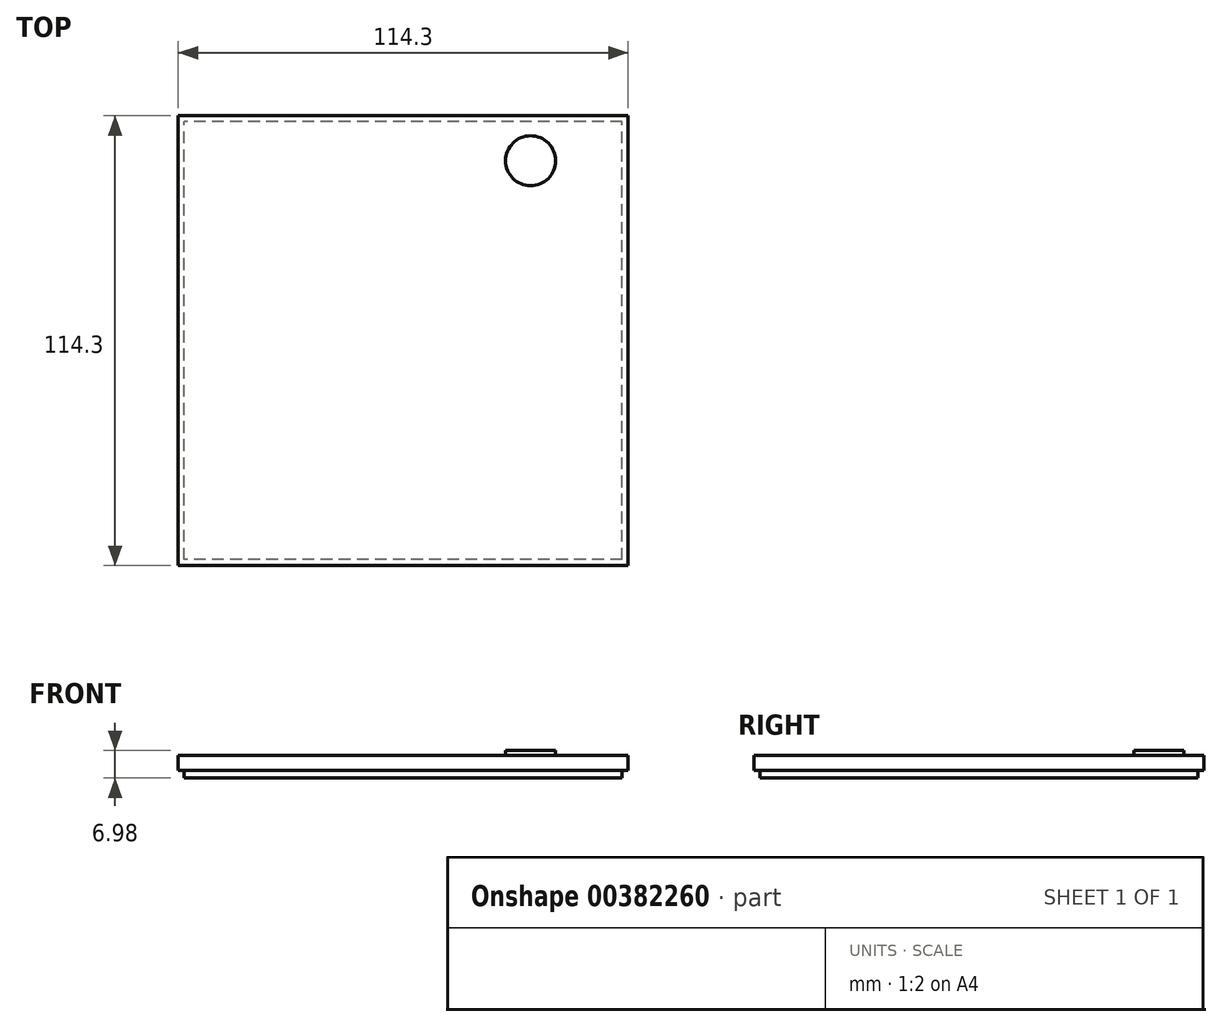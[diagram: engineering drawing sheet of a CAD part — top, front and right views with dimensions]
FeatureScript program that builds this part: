
annotation { "Feature Type Name" : "Feature", "Feature Type Description" : "" }
export const myFeature = defineFeature(function(context is Context, id is Id, definition is map)
    precondition{}
    {
        {
            var Q0;
            Q0=qCreatedBy(makeId("Top.planeOp"),FACE);
            var sketch = newSketch(context, id + "F0", { "sketchPlane" : qUnion([Q0])});
            skLineSegment(sketch, "E0.bottom", {"start": v(57.15, 57.15) * mm, "end": v(-57.15, 57.15) * mm});
            skLineSegment(sketch, "E0.top", {"start": v(57.15, -57.15) * mm, "end": v(-57.15, -57.15) * mm});
            skLineSegment(sketch, "E0.left", {"start": v(57.15, 57.15) * mm, "end": v(57.15, -57.15) * mm});
            skLineSegment(sketch, "E0.right", {"start": v(-57.15, 57.15) * mm, "end": v(-57.15, -57.15) * mm});
            skPoint(sketch, "E0.middle", {"position": v(0, 0) * mm});
            skSolve(sketch);
        }
        {
            var Q0;
            Q0=makeQuery(id+"F0.imprint","IMPRINT",FACE,{"disambiguationData":[TD([[makeQuery(id+"F0.imprint","IMPRINT",EDGE,{"derivedFrom":sQuery(id+"F0.wireOp",EDGE,"E0.bottom")}),1.0]])]});
            extrude(context, id + "F1", {"entities" : qUnion([Q0]), "depth" : 2.54 * mm});
        }
        {
            var Q0;
            Q0=makeQuery(id+"F1.opExtrude","SWEPT_FACE",FACE,{"disambiguationData":[OSD([sQuery(id+"F0.wireOp",EDGE,"E0.left")])]});
            var sketch = newSketch(context, id + "F2", { "sketchPlane" : qUnion([Q0])});
            skLineSegment(sketch, "E1.bottom", {"start": v(-57.15, 0) * mm, "end": v(57.15, 0) * mm});
            skLineSegment(sketch, "E2.top", {"start": v(-57.15, 27.94) * mm, "end": v(57.15, 27.94) * mm});
            skLineSegment(sketch, "E2.left", {"start": v(-57.15, 2.54) * mm, "end": v(-57.15, 27.94) * mm});
            skLineSegment(sketch, "E2.right", {"start": v(57.15, 2.54) * mm, "end": v(57.15, 27.94) * mm});
            skSolve(sketch);
        }
        {
            var Q0;
            Q0=makeQuery(id+"F2.imprint","IMPRINT",FACE,{"disambiguationData":[TD([[makeQuery(id+"F2.imprint","IMPRINT",EDGE,{"derivedFrom":sQuery(id+"F2.wireOp",EDGE,"E2.top")}),-1.0]])]});
            extrude(context, id + "F3", {"entities" : qUnion([Q0]), "oppositeDirection" : true, "depth" : 2.54 * mm});
        }
        {
            var Q0;
            Q0=makeQuery(id+"F3.opExtrude","SWEPT_BODY",BODY,{"disambiguationData":[OSD([sQuery(id+"F0.wireOp",EDGE,"E0.left"),sQuery(id+"F2.wireOp",EDGE,"E2.top"),sQuery(id+"F2.wireOp",EDGE,"E2.left"),sQuery(id+"F2.wireOp",EDGE,"E2.right")])]});
            var Q1;
            Q1=qCreatedBy(makeId("Right.planeOp"),FACE);
            mirror(context, id + "F4", {"operationType" : NewBodyOperationType.ADD, "entities" : qUnion([Q0]), "mirrorPlane" : qUnion([Q1])});
        }
        {
            var Q0;
            {var subQ0=makeQuery(id+"F3.opExtrude","SWEPT_FACE",FACE,{"disambiguationData":[OSD([sQuery(id+"F2.wireOp",EDGE,"E2.right")])]});Q0=makeQuery(id+"F4.boolean.opBoolean","MERGE",FACE,{"derivedFrom":[makeQuery(id+"F1.opExtrude","SWEPT_FACE",FACE,{"disambiguationData":[OSD([sQuery(id+"F0.wireOp",EDGE,"E0.bottom")])]}),subQ0,makeQuery(id+"F4.opPattern","COPY",FACE,{"derivedFrom":subQ0,"instanceName":"1"})]});}
            var sketch = newSketch(context, id + "F5", { "sketchPlane" : qUnion([Q0])});
            skLineSegment(sketch, "E3.bottom", {"start": v(-54.61, 2.54) * mm, "end": v(54.61, 2.54) * mm});
            skLineSegment(sketch, "E3.top", {"start": v(-54.61, 27.94) * mm, "end": v(54.61, 27.94) * mm});
            skLineSegment(sketch, "E3.left", {"start": v(-54.61, 2.54) * mm, "end": v(-54.61, 27.94) * mm});
            skLineSegment(sketch, "E3.right", {"start": v(54.61, 2.54) * mm, "end": v(54.61, 27.94) * mm});
            skSolve(sketch);
        }
        {
            var Q0;
            Q0=makeQuery(id+"F5.imprint","IMPRINT",FACE,{"disambiguationData":[TD([[makeQuery(id+"F5.imprint","IMPRINT",EDGE,{"derivedFrom":sQuery(id+"F5.wireOp",EDGE,"E3.bottom")}),1.0]])]});
            extrude(context, id + "F6", {"entities" : qUnion([Q0]), "oppositeDirection" : true, "depth" : 2.54 * mm});
        }
        {
            var Q0;
            Q0=makeQuery(id+"F6.opExtrude","SWEPT_BODY",BODY,{"disambiguationData":[OSD([sQuery(id+"F5.wireOp",EDGE,"E3.bottom"),sQuery(id+"F5.wireOp",EDGE,"E3.top"),sQuery(id+"F5.wireOp",EDGE,"E3.left"),sQuery(id+"F5.wireOp",EDGE,"E3.right")])]});
            var Q1;
            Q1=qCreatedBy(makeId("Front.planeOp"),FACE);
            mirror(context, id + "F7", {"operationType" : NewBodyOperationType.ADD, "entities" : qUnion([Q0]), "mirrorPlane" : qUnion([Q1])});
        }
        {
            var Q0;
            {var subQ0=makeQuery(id+"F6.opExtrude","SWEPT_FACE",FACE,{"disambiguationData":[OSD([sQuery(id+"F5.wireOp",EDGE,"E3.top")])]});var subQ1=makeQuery(id+"F3.opExtrude","SWEPT_FACE",FACE,{"disambiguationData":[OSD([sQuery(id+"F2.wireOp",EDGE,"E2.top")])]});Q0=makeQuery(id+"F7.boolean.opBoolean","MERGE",FACE,{"derivedFrom":[subQ1,makeQuery(id+"F4.opPattern","COPY",FACE,{"derivedFrom":subQ1,"instanceName":"1"}),subQ0,makeQuery(id+"F7.opPattern","COPY",FACE,{"derivedFrom":subQ0,"instanceName":"1"})]});}
            var sketch = newSketch(context, id + "F8", { "sketchPlane" : qUnion([Q0])});
            skLineSegment(sketch, "E4.bottom", {"start": v(57.15, 57.15) * mm, "end": v(-57.15, 57.15) * mm});
            skLineSegment(sketch, "E4.top", {"start": v(57.15, -57.15) * mm, "end": v(-57.15, -57.15) * mm});
            skLineSegment(sketch, "E4.left", {"start": v(57.15, 57.15) * mm, "end": v(57.15, -57.15) * mm});
            skLineSegment(sketch, "E4.right", {"start": v(-57.15, 57.15) * mm, "end": v(-57.15, -57.15) * mm});
            skSolve(sketch);
        }
        {
            var Q0;
            Q0=makeQuery(id+"F8.imprint","IMPRINT",FACE,{"disambiguationData":[TD([[makeQuery(id+"F8.imprint","IMPRINT",EDGE,{"derivedFrom":sQuery(id+"F8.wireOp",EDGE,"E4.bottom")}),-1.0]])]});
            var Q1;
            {var subQ0=makeQuery(id+"F6.opExtrude","CAP_EDGE",EDGE,{"disambiguationData":[OSD([sQuery(id+"F5.wireOp",EDGE,"E3.top")])],"isStart":false});Q1=makeQuery(id+"F8.imprint","IMPRINT",FACE,{"disambiguationData":[TD([[makeQuery(id+"F8.imprint","IMPRINT",EDGE,{"derivedFrom":subQ0}),1.0]])]});}
            extrude(context, id + "F9", {"entities" : qUnion([Q0, Q1]), "depth" : 2.54 * mm});
        }
        {
            var Q0;
            Q0=makeQuery(id+"F9.opExtrude","CAP_FACE",FACE,{"disambiguationData":[OSD([sQuery(id+"F8.wireOp",EDGE,"E4.bottom"),sQuery(id+"F8.wireOp",EDGE,"E4.top"),sQuery(id+"F8.wireOp",EDGE,"E4.left"),sQuery(id+"F8.wireOp",EDGE,"E4.right")])],"isStart":false});
            var sketch = newSketch(context, id + "F10", { "sketchPlane" : qUnion([Q0])});
            skLineSegment(sketch, "E5.bottom", {"start": v(57.15, 57.15) * mm, "end": v(-57.15, 57.15) * mm});
            skLineSegment(sketch, "E5.top", {"start": v(57.15, -57.15) * mm, "end": v(-57.15, -57.15) * mm});
            skLineSegment(sketch, "E5.left", {"start": v(57.15, 57.15) * mm, "end": v(57.15, -57.15) * mm});
            skLineSegment(sketch, "E5.right", {"start": v(-57.15, 57.15) * mm, "end": v(-57.15, -57.15) * mm});
            skSolve(sketch);
        }
        {
            var Q0;
            Q0=makeQuery(id+"F10.imprint","IMPRINT",FACE,{"disambiguationData":[TD([[makeQuery(id+"F10.imprint","IMPRINT",EDGE,{"derivedFrom":sQuery(id+"F10.wireOp",EDGE,"E5.bottom")}),-1.0]])]});
            extrude(context, id + "F11", {"entities" : qUnion([Q0]), "operationType" : NewBodyOperationType.ADD, "depth" : 2.54 * mm});
        }
        {
            var Q0;
            Q0=makeQuery(id+"F11.opExtrude","CAP_FACE",FACE,{"disambiguationData":[OSD([sQuery(id+"F10.wireOp",EDGE,"E5.bottom"),sQuery(id+"F10.wireOp",EDGE,"E5.top"),sQuery(id+"F10.wireOp",EDGE,"E5.left"),sQuery(id+"F10.wireOp",EDGE,"E5.right")])],"isStart":false});
            var sketch = newSketch(context, id + "F12", { "sketchPlane" : qUnion([Q0])});
            skLineSegment(sketch, "E6.bottom", {"start": v(-57.15, 57.15) * mm, "end": v(-52.07, 57.15) * mm});
            skLineSegment(sketch, "E6.top", {"start": v(-57.15, 52.07) * mm, "end": v(-52.07, 52.07) * mm});
            skLineSegment(sketch, "E6.left", {"start": v(-57.15, 57.15) * mm, "end": v(-57.15, 52.07) * mm});
            skLineSegment(sketch, "E6.right", {"start": v(-52.07, 57.15) * mm, "end": v(-52.07, 52.07) * mm});
            skLineSegment(sketch, "E7.bottom", {"start": v(-52.07, 52.07) * mm, "end": v(24.13, 52.07) * mm});
            skLineSegment(sketch, "E7.top", {"start": v(-52.07, -52.07) * mm, "end": v(24.13, -52.07) * mm});
            skLineSegment(sketch, "E7.left", {"start": v(-52.07, 52.07) * mm, "end": v(-52.07, -52.07) * mm});
            skLineSegment(sketch, "E7.right", {"start": v(24.13, 52.07) * mm, "end": v(24.13, -52.07) * mm});
            skSolve(sketch);
        }
        {
            var Q0;
            Q0=makeQuery(id+"F12.imprint","IMPRINT",FACE,{"disambiguationData":[TD([[makeQuery(id+"F12.imprint","IMPRINT",EDGE,{"derivedFrom":sQuery(id+"F12.wireOp",EDGE,"E7.bottom")}),-1.0]])]});
            extrude(context, id + "F13", {"entities" : qUnion([Q0]), "operationType" : NewBodyOperationType.REMOVE, "oppositeDirection" : true, "depth" : 1.27 * mm});
        }
        {
            var Q0;
            Q0=makeQuery(id+"F11.opExtrude","CAP_FACE",FACE,{"disambiguationData":[OSD([sQuery(id+"F10.wireOp",EDGE,"E5.bottom"),sQuery(id+"F10.wireOp",EDGE,"E5.top"),sQuery(id+"F10.wireOp",EDGE,"E5.left"),sQuery(id+"F10.wireOp",EDGE,"E5.right")])],"isStart":false});
            var sketch = newSketch(context, id + "F14", { "sketchPlane" : qUnion([Q0])});
            skLineSegment(sketch, "E8", {"start": v(0, 0) * mm, "end": v(40.64, 0) * mm, "construction": true});
            skPoint(sketch, "E8.endSnap0", {"position": v(24.13, 0) * mm});
            skCircle(sketch, "E9", {"center": v(40.64, 0) * mm, "radius": 6.35 * mm});
            skLineSegment(sketch, "E10", {"start": v(40.64, 0) * mm, "end": v(40.64, 45.72) * mm});
            skLineSegment(sketch, "E11", {"start": v(40.64, 45.72) * mm, "end": v(48.9, 45.72) * mm});
            skCircle(sketch, "E12", {"center": v(48.9, 45.72) * mm, "radius": 6.35 * mm});
            skCircle(sketch, "E13.MirrorC", {"center": v(32.39, 45.72) * mm, "radius": 6.35 * mm});
            skSolve(sketch);
        }
        {
            var Q0;
            Q0=makeQuery(id+"F14.imprint","IMPRINT",FACE,{"disambiguationData":[TD([[makeQuery(id+"F14.imprint","IMPRINT",EDGE,{"derivedFrom":sQuery(id+"F14.wireOp",EDGE,"E12")}),1.0]])]});
            var Q1;
            Q1=makeQuery(id+"F14.imprint","IMPRINT",FACE,{"disambiguationData":[TD([[makeQuery(id+"F14.imprint","IMPRINT",EDGE,{"derivedFrom":sQuery(id+"F14.wireOp",EDGE,"E13.MirrorC")}),-1.0]])]});
            var Q2;
            Q2=makeQuery(id+"F14.imprint","IMPRINT",FACE,{"disambiguationData":[TD([[makeQuery(id+"F14.imprint","IMPRINT",EDGE,{"derivedFrom":sQuery(id+"F14.wireOp",EDGE,"E9")}),1.0]])]});
            extrude(context, id + "F15", {"entities" : qUnion([Q0, Q1, Q2]), "operationType" : NewBodyOperationType.REMOVE, "oppositeDirection" : true, "depth" : 1.27 * mm});
        }
        {
            var Q0;
            Q0=makeQuery(id+"F1.opExtrude","SWEPT_BODY",BODY,{"disambiguationData":[OSD([sQuery(id+"F0.wireOp",EDGE,"E0.bottom"),sQuery(id+"F0.wireOp",EDGE,"E0.top"),sQuery(id+"F0.wireOp",EDGE,"E0.left"),sQuery(id+"F0.wireOp",EDGE,"E0.right")])]});
            deleteBodies(context, id + "F16", {"entities" : qUnion([Q0])});
        }
        {
            var Q0;
            Q0=makeQuery(id+"F9.opExtrude","CAP_FACE",FACE,{"disambiguationData":[OSD([sQuery(id+"F8.wireOp",EDGE,"E4.bottom"),sQuery(id+"F8.wireOp",EDGE,"E4.top"),sQuery(id+"F8.wireOp",EDGE,"E4.left"),sQuery(id+"F8.wireOp",EDGE,"E4.right")])],"isStart":true});
            var sketch = newSketch(context, id + "F17", { "sketchPlane" : qUnion([Q0])});
            skLineSegment(sketch, "E14.bottom", {"start": v(55.63, 55.63) * mm, "end": v(-55.63, 55.63) * mm});
            skLineSegment(sketch, "E14.top", {"start": v(55.63, -55.63) * mm, "end": v(-55.63, -55.63) * mm});
            skLineSegment(sketch, "E14.left", {"start": v(55.63, 55.63) * mm, "end": v(55.63, -55.63) * mm});
            skLineSegment(sketch, "E14.right", {"start": v(-55.63, 55.63) * mm, "end": v(-55.63, -55.63) * mm});
            skPoint(sketch, "E14.middle", {"position": v(0, 0) * mm});
            skSolve(sketch);
        }
        {
            var Q0;
            Q0=makeQuery(id+"F17.imprint","IMPRINT",FACE,{"disambiguationData":[TD([[makeQuery(id+"F17.imprint","IMPRINT",EDGE,{"derivedFrom":sQuery(id+"F17.wireOp",EDGE,"E14.bottom")}),1.0]])]});
            extrude(context, id + "F18", {"entities" : qUnion([Q0]), "depth" : 1.9 * mm});
        }
    });
